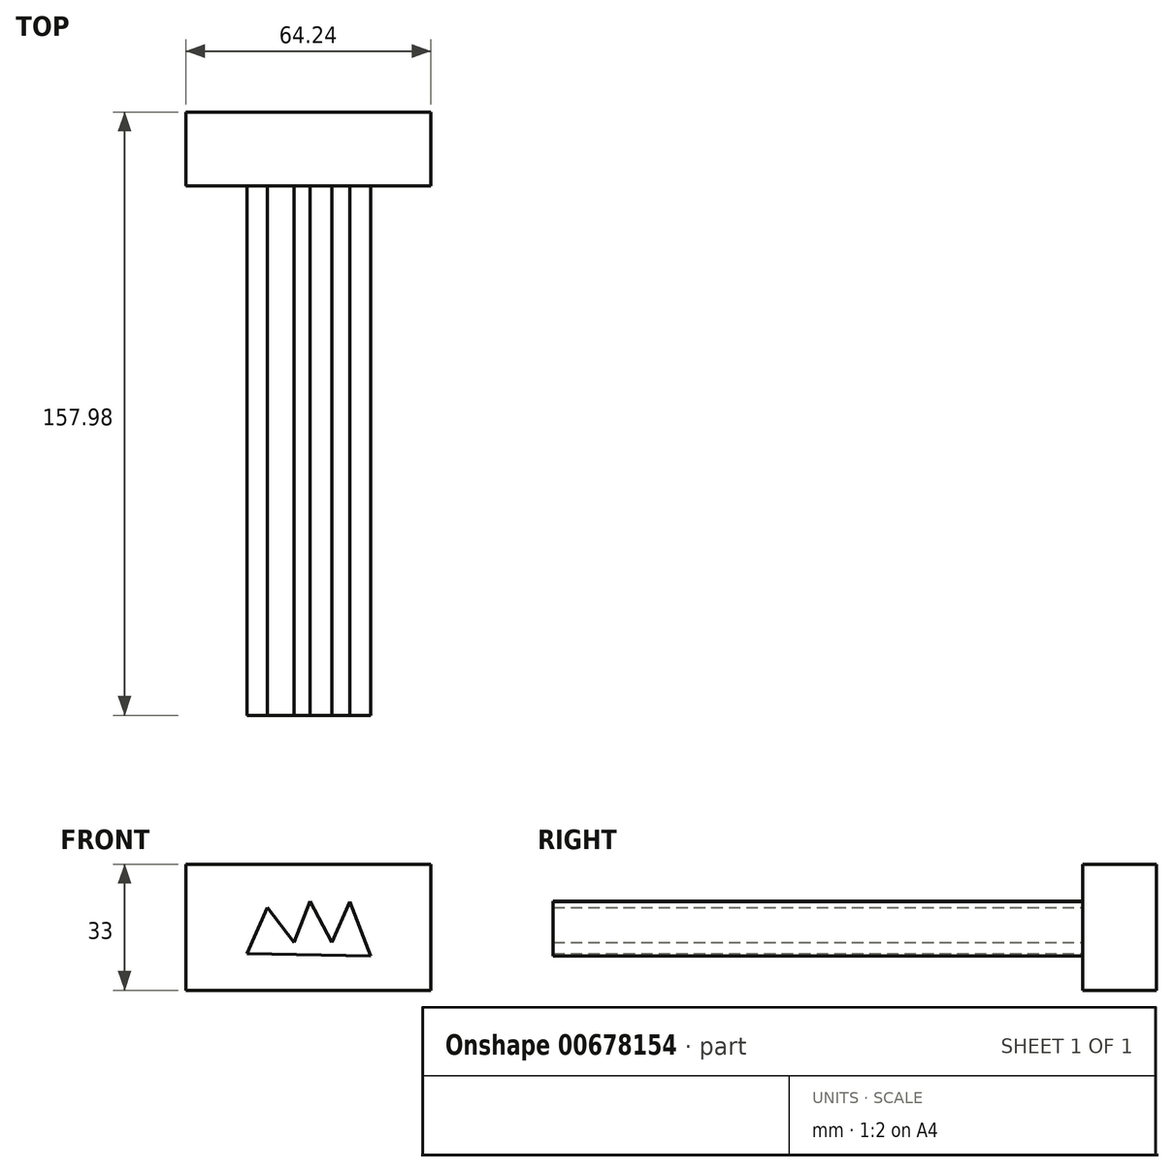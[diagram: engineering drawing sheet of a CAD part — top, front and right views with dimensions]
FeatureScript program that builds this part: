
annotation { "Feature Type Name" : "Feature", "Feature Type Description" : "" }
export const myFeature = defineFeature(function(context is Context, id is Id, definition is map)
    precondition{}
    {
        {
            var Q0;
            Q0=qCreatedBy(makeId("Front.planeOp"),FACE);
            var sketch = newSketch(context, id + "F0", { "sketchPlane" : qUnion([Q0])});
            skLineSegment(sketch, "E0", {"start": v(-16.53, -6.36) * mm, "end": v(-11.21, 5.7) * mm});
            skLineSegment(sketch, "E1", {"start": v(-11.21, 5.7) * mm, "end": v(-4.23, -3.44) * mm});
            skLineSegment(sketch, "E2", {"start": v(-4.23, -3.44) * mm, "end": v(-0.02, 7.36) * mm});
            skLineSegment(sketch, "E3", {"start": v(-0.02, 7.36) * mm, "end": v(5.7, -3.44) * mm});
            skLineSegment(sketch, "E4", {"start": v(5.7, -3.44) * mm, "end": v(10.43, 7.24) * mm});
            skLineSegment(sketch, "E5", {"start": v(10.43, 7.24) * mm, "end": v(15.87, -7.07) * mm});
            skLineSegment(sketch, "E6", {"start": v(15.87, -7.07) * mm, "end": v(-16.53, -6.36) * mm});
            skSolve(sketch);
        }
        {
            var Q0;
            Q0=makeQuery(id+"F0.imprint","IMPRINT",FACE,{"disambiguationData":[TD([[makeQuery(id+"F0.imprint","IMPRINT",EDGE,{"derivedFrom":sQuery(id+"F0.wireOp",EDGE,"E0")}),-1.0]])]});
            var Q1;
            Q1=sQuery(id+"F0.wireOp",EDGE,"E0");
            var Q2;
            Q2=sQuery(id+"F0.wireOp",EDGE,"E1");
            var Q3;
            Q3=sQuery(id+"F0.wireOp",EDGE,"E2");
            var Q4;
            Q4=sQuery(id+"F0.wireOp",EDGE,"E3");
            var Q5;
            Q5=sQuery(id+"F0.wireOp",EDGE,"E4");
            var Q6;
            Q6=sQuery(id+"F0.wireOp",EDGE,"E5");
            var Q7;
            Q7=sQuery(id+"F0.wireOp",EDGE,"E6");
            extrude(context, id + "F1", {"entities" : qUnion([Q0]), "surfaceEntities" : qUnion([Q1, Q2, Q3, Q4, Q5, Q6, Q7]), "depth" : 150 * mm, "offsetDistance" : 25 * mm});
        }
        {
            var Q0;
            Q0=qCreatedBy(makeId("Top.planeOp"),FACE);
            var sketch = newSketch(context, id + "F2", { "sketchPlane" : qUnion([Q0])});
            skLineSegment(sketch, "E7.bottom", {"start": v(-32.55, 7.98) * mm, "end": v(31.69, 7.98) * mm});
            skLineSegment(sketch, "E7.top", {"start": v(-32.55, -11.42) * mm, "end": v(31.69, -11.42) * mm});
            skLineSegment(sketch, "E7.left", {"start": v(-32.55, 7.98) * mm, "end": v(-32.55, -11.42) * mm});
            skLineSegment(sketch, "E7.right", {"start": v(31.69, 7.98) * mm, "end": v(31.69, -11.42) * mm});
            skSolve(sketch);
        }
        {
            var Q0;
            Q0=makeQuery(id+"F2.imprint","IMPRINT",FACE,{"disambiguationData":[TD([[makeQuery(id+"F2.imprint","IMPRINT",EDGE,{"derivedFrom":sQuery(id+"F2.wireOp",EDGE,"E7.bottom")}),-1.0]])]});
            extrude(context, id + "F3", {"entities" : qUnion([Q0]), "operationType" : NewBodyOperationType.ADD, "depth" : 17 * mm, "offsetDistance" : 25 * mm, "hasSecondDirection" : true, "secondDirectionOppositeDirection" : true, "secondDirectionDepth" : 16 * mm});
        }
    });
